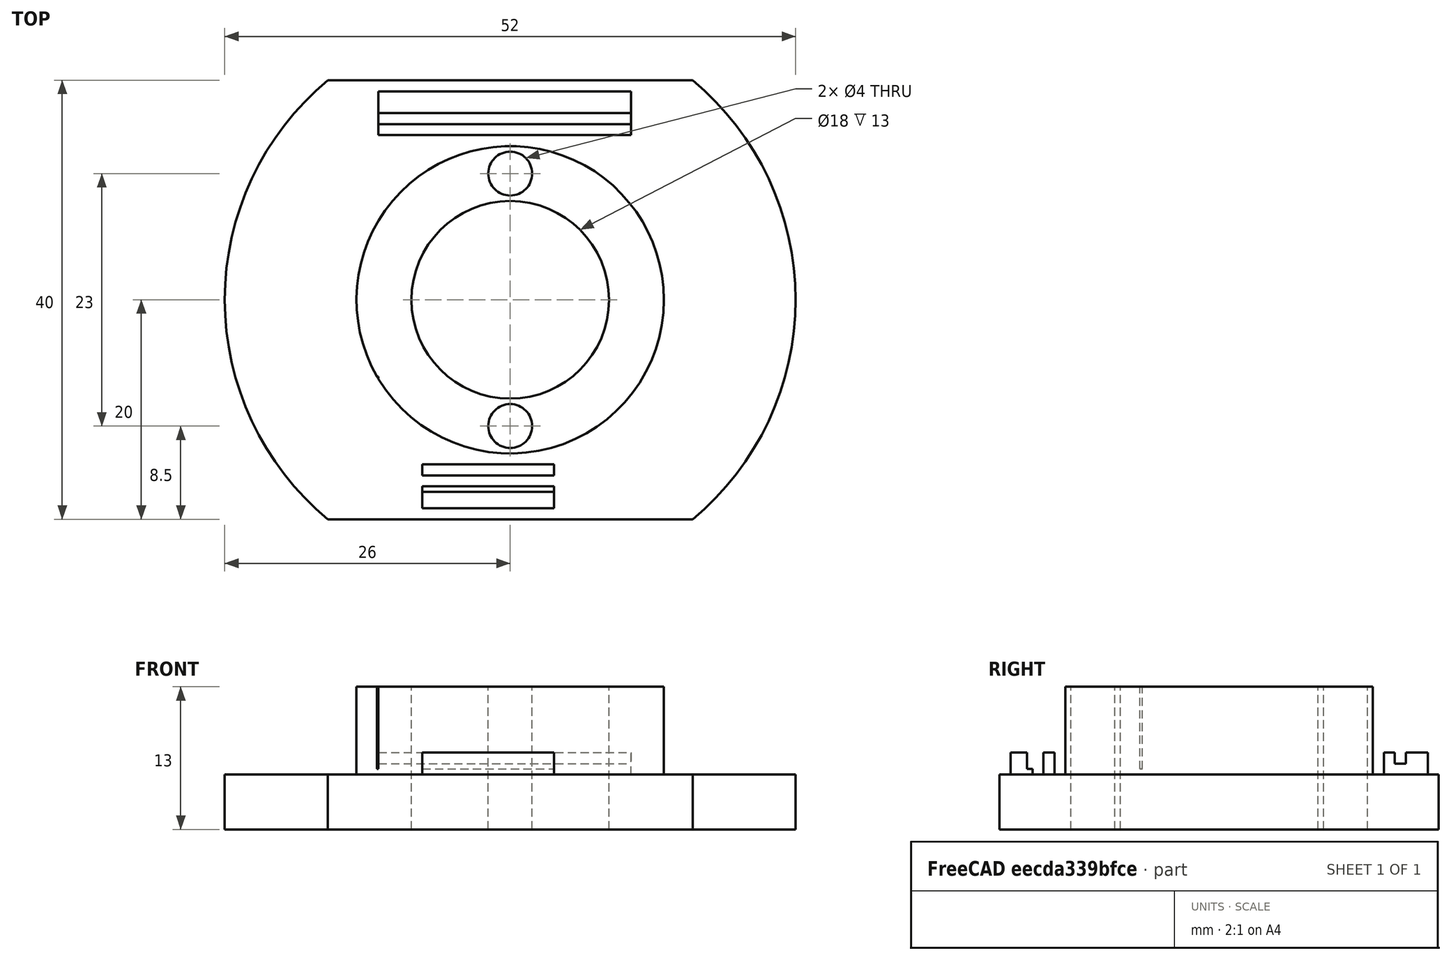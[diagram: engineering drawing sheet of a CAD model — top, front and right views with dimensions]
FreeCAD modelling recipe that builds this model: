
FCSTD DOCUMENT  (FreeCAD 0.15R4671 (Git))
Label: Ferma Fazzolettone
License: All rights reserved
LicenseURL: http://en.wikipedia.org/wiki/All_rights_reserved
objects: Part::Box×10, Part::Cut×8, Part::Cylinder×6, Part::MultiFuse×5, App::DocumentObjectGroup×1
note: 29 computed .brp shape members not serialized (recipe doc carries the construction recipe); baked Part::Feature solids carry a one-line shape summary decoded from their .brp

FEATURE [Part::Box] Box  label="Cubo"
  Height = 14
  Length = 25
  Width = 1
FEATURE [Part::Box] Box001  label="Cubo001"
  Height = 13
  Length = 23
  Placement = pos=(0.5,-0.5,0.5) rot=(0,0,1;0rad)
  Width = 1
FEATURE [Part::Box] Box002  label="Cubo002"
  Height = 13
  Length = 5
  Placement = pos=(1,0,0.5) rot=(0,0,1;0rad)
  Width = 10
FEATURE [Part::MultiFuse] Fusion  label="ESP-01"
  Placement = pos=(5,2,0) rot=(0,0,1;0rad)
  Shapes = -> [Box,Box002,Box001]
FEATURE [App::DocumentObjectGroup] Gruppo
FEATURE [Part::Box] Box003  label="Cubo003"
  Height = 12
  Length = 38
  Width = 1
FEATURE [Part::Box] Box004  label="Cubo004"
  Height = 10
  Length = 34
  Placement = pos=(3,-0.5,1) rot=(0,0,1;0rad)
  Width = 1
FEATURE [Part::MultiFuse] Fusion001  label="Display"
  Placement = pos=(4,36,13) rot=(1,0,0;3.14159rad)
  Shapes = -> [Box004,Box003]
FEATURE [Part::Cylinder] Cylinder  label="Cilindro"
  Angle = 360
  Height = 28
  Placement = pos=(23,19,-7) rot=(0,0,1;0rad)
  Radius = 9
FEATURE [Part::Cylinder] Cylinder001  label="Cilindro001"
  Angle = 360
  Height = 14
  Placement = pos=(23,19,0) rot=(0,0,1;0rad)
  Radius = 14
FEATURE [Part::Cylinder] Cylinder002  label="Cilindro002"
  Angle = 360
  Height = 5
  Placement = pos=(23,19,-5) rot=(0,0,1;0rad)
  Radius = 26
FEATURE [Part::Cylinder] Cylinder003  label="Cilindro003"
  Angle = 360
  Height = 5
  Placement = pos=(23,19,14) rot=(0,0,1;0rad)
  Radius = 26
FEATURE [Part::MultiFuse] Fusion002
  Shapes = -> [Cylinder003,Cylinder002,Cylinder001]
FEATURE [Part::Cut] Cut
  Base = -> Fusion002
  Tool = -> Cylinder
FEATURE [Part::Box] Box005  label="Cubo005"
  Height = 2
  Length = 23
  Placement = pos=(11,34,0) rot=(0,0,1;0rad)
  Width = 4
FEATURE [Part::MultiFuse] Fusion003
  Shapes = -> [Box005,Cut]
FEATURE [Part::Cut] Cut001
  Base = -> Fusion003
  Tool = -> Fusion001
FEATURE [Part::Box] Box006  label="Cubo006"
  Height = 2
  Length = 12
  Placement = pos=(15,0,0) rot=(0,0,1;0rad)
  Width = 4
FEATURE [Part::Box] Box007  label="Cubo007"
  Height = 10
  Length = 46
  Placement = pos=(0,-11,-6) rot=(0,0,1;0rad)
  Width = 10
FEATURE [Part::MultiFuse] Fusion004
  Shapes = -> [Box006,Cut001]
FEATURE [Part::Cut] Cut002
  Base = -> Fusion004
  Tool = -> Fusion
FEATURE [Part::Box] Box008  label="Cubo008"
  Height = 15
  Length = 54
  Placement = pos=(-4,-8,8) rot=(0,0,1;0rad)
  Width = 53
FEATURE [Part::Cut] Cut003
  Base = -> Cut002
  Tool = -> Box008
FEATURE [Part::Cut] Cut004
  Base = -> Cut003
  Tool = -> Box007
FEATURE [Part::Box] Box009  label="Cubo009"
  Height = 10
  Length = 46
  Placement = pos=(0,39,-6) rot=(0,0,1;0rad)
  Width = 10
FEATURE [Part::Cut] Cut005
  Base = -> Cut004
  Tool = -> Box009
FEATURE [Part::Cylinder] Cylinder004  label="Cilindro004"
  Angle = 360
  Height = 22
  Placement = pos=(23,7.5,-10) rot=(0,0,1;0rad)
  Radius = 2
FEATURE [Part::Cylinder] Cylinder005  label="Cilindro005"
  Angle = 360
  Height = 22
  Placement = pos=(23,30.5,-10) rot=(0,0,1;0rad)
  Radius = 2
FEATURE [Part::Cut] Cut006
  Base = -> Cut005
  Tool = -> Cylinder005
FEATURE [Part::Cut] Cut007
  Base = -> Cut006
  Tool = -> Cylinder004
